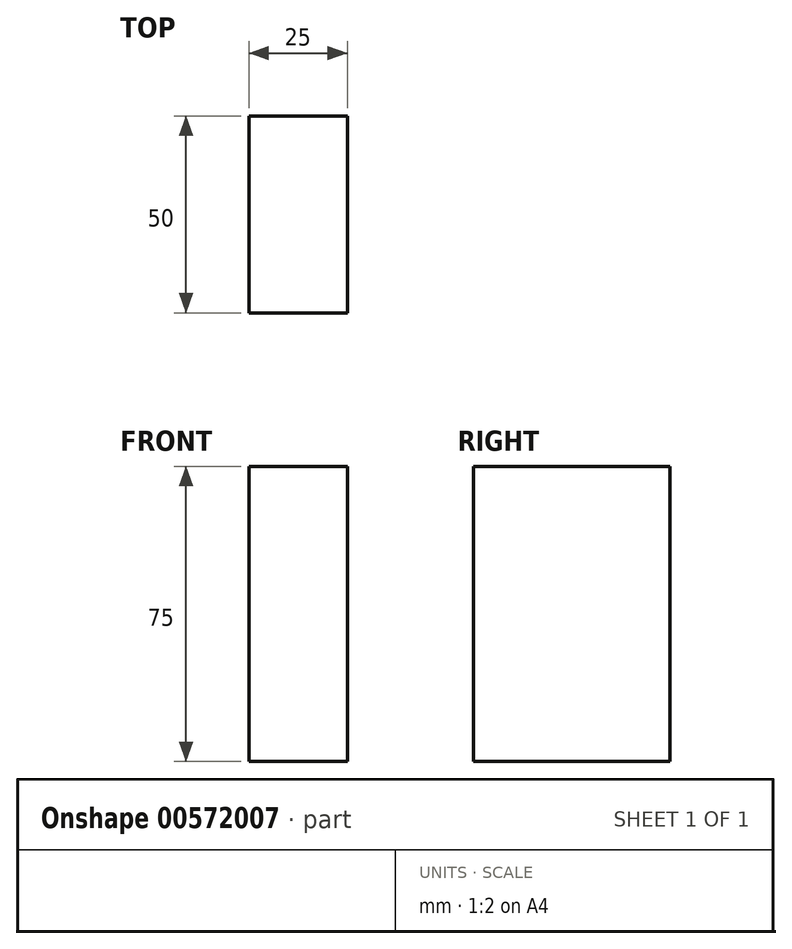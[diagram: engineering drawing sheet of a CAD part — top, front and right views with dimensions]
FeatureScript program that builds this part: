
annotation { "Feature Type Name" : "Feature", "Feature Type Description" : "" }
export const myFeature = defineFeature(function(context is Context, id is Id, definition is map)
    precondition{}
    {
        {
            var Q0;
            Q0=qCreatedBy(makeId("Top.planeOp"),FACE);
            var sketch = newSketch(context, id + "F0", { "sketchPlane" : qUnion([Q0])});
            skLineSegment(sketch, "E0.bottom", {"start": v(-12.5, 25) * mm, "end": v(12.5, 25) * mm});
            skLineSegment(sketch, "E0.top", {"start": v(-12.5, -25) * mm, "end": v(12.5, -25) * mm});
            skLineSegment(sketch, "E0.left", {"start": v(-12.5, 25) * mm, "end": v(-12.5, -25) * mm});
            skLineSegment(sketch, "E0.right", {"start": v(12.5, 25) * mm, "end": v(12.5, -25) * mm});
            skPoint(sketch, "E0.middle", {"position": v(0, 0) * mm});
            skSolve(sketch);
        }
        {
            var Q0;
            Q0=makeQuery(id+"F0.imprint","IMPRINT",FACE,{"disambiguationData":[TD([[makeQuery(id+"F0.imprint","IMPRINT",EDGE,{"derivedFrom":sQuery(id+"F0.wireOp",EDGE,"E0.bottom")}),-1.0]])]});
            extrude(context, id + "F1", {"entities" : qUnion([Q0]), "depth" : 75 * mm, "offsetDistance" : 25 * mm});
        }
    });
